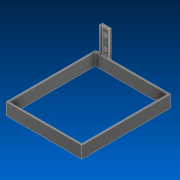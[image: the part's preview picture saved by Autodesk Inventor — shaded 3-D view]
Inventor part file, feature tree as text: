
AUTODESK INVENTOR PART (.ipt)
format: ipt  version: 2022.2 (Build 262287000, 287)  size: 174,080 bytes
history: native  units: in
note: dims shown in document units (in); Inventor stores cm internally (conversion verified against a paired STEP export)
features: sketch x2, extrude x2, fillet x2, hole x1, projected_geometry x1
ambient origin geometry x8: Origin, YZ Plane, XZ Plane, XY Plane, X Axis, Y Axis, Z Axis, Center Point
bodies: Solid1 (feature_tree)
feature tree (8):
  sketch  "Sketch1"  dims[d2=6.0in d3=7.1in]
  extrude  "Extrusion1"  Depth=7.1in
  extrude  "Extrusion5"  Depth=0.225in
  hole  "Hole2"  [1 undecoded]
  fillet  "Fillet3"  Radius=0.01in
  fillet  "Fillet4"  Radius=0.5in
  sketch  "Sketch6"  dims[d4=1.0in d5=0.0in d29=0.125in d30=0.125in d32=0.01in d33=0.5in d37=1.0in d39=0.175in d40=0.75in d41=0.35in d42=0.1in d43=0.5635in d44=1.0in d45=0.8108in d46=0.5in d47=0.5in d48=0.1in d49=0.825in d50=2.0in d51=0.0in d52=0.5in d53=0.125in d54=0.225in]
  projected_geometry  "Projected Loop3"
note: 1 required parameter value undecoded (feature->parameter linkage not recoverable at this tier; creation-order binding heuristic only, values carry confidence <= 0.55)
